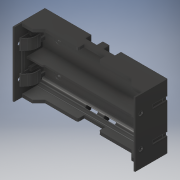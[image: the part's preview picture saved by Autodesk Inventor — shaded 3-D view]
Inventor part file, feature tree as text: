
AUTODESK INVENTOR PART (.ipt)
format: ipt  version: 2019 (Build 230136000, 136)  size: 366,592 bytes
history: native  units: mm
features: extrude x3, sketch x3, other x2
ambient origin geometry x8: Origin, YZ Plane, XZ Plane, XY Plane, X Axis, Y Axis, Z Axis, Center Point
bodies: Body1 (feature_tree)
feature tree (8):
  other  "Твердое тело1"
  extrude  "Выдавливание1"  Depth=1.0mm TaperAngle=0.0deg
  extrude  "Выдавливание2"  Depth=1.0mm TaperAngle=0.0deg
  extrude  "Выдавливание3"  Depth=20.0mm TaperAngle=0.0deg
  sketch  "Эскиз1"
  sketch  "Эскиз2"
  sketch  "Эскиз3"
  other  "Corps principal"
